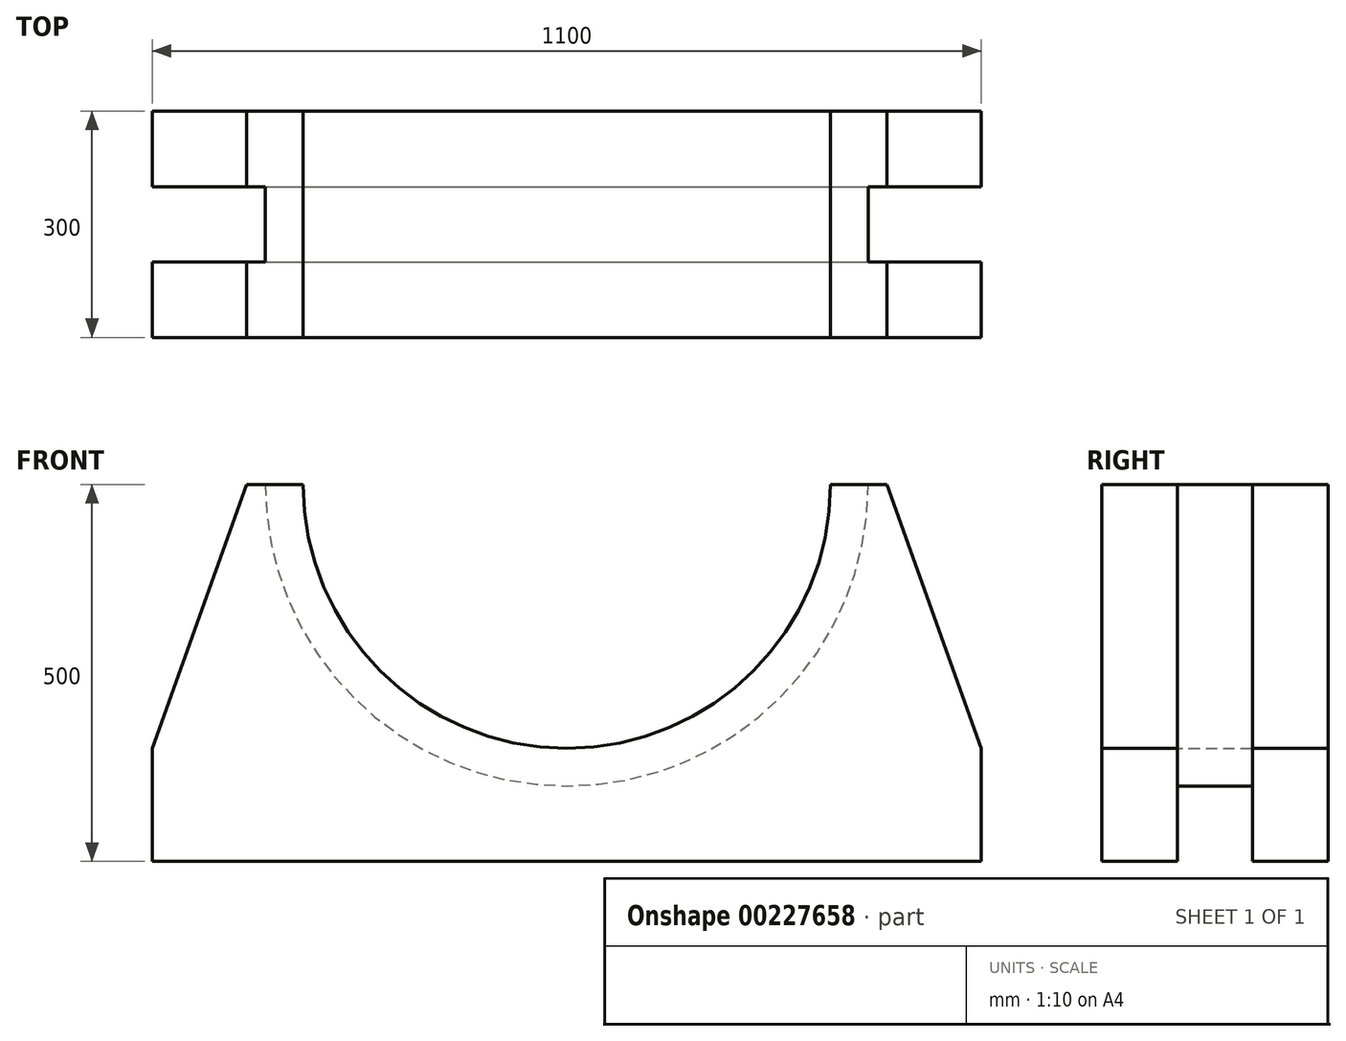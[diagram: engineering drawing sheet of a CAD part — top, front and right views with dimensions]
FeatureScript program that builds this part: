
annotation { "Feature Type Name" : "Feature", "Feature Type Description" : "" }
export const myFeature = defineFeature(function(context is Context, id is Id, definition is map)
    precondition{}
    {
        {
            var Q0;
            Q0=qCreatedBy(makeId("Front.planeOp"),FACE);
            var sketch = newSketch(context, id + "F0", { "sketchPlane" : qUnion([Q0])});
            skArc(sketch, "E0", {"start": v(-350, 0) * mm, "mid": v(-247.49, -247.49) * mm, "end": v(0, -350) * mm});
            skLineSegment(sketch, "E1", {"start": v(0, -696.52) * mm, "end": v(0, 518.58) * mm, "construction": true});
            skLineSegment(sketch, "E2", {"start": v(-350, 0) * mm, "end": v(-425, 0) * mm});
            skLineSegment(sketch, "E3", {"start": v(-425, 0) * mm, "end": v(-550, -350) * mm});
            skLineSegment(sketch, "E4", {"start": v(-550, -350) * mm, "end": v(-550, -500) * mm});
            skLineSegment(sketch, "E5", {"start": v(-550, -500) * mm, "end": v(0, -500) * mm});
            skLineSegment(sketch, "E6", {"start": v(0, -500) * mm, "end": v(0, -350) * mm});
            skLineSegment(sketch, "E7.MirrorCS", {"start": v(350, 0) * mm, "end": v(425, 0) * mm});
            skLineSegment(sketch, "E8.MirrorCS", {"start": v(550, -350) * mm, "end": v(550, -500) * mm});
            skLineSegment(sketch, "E9.MirrorCS", {"start": v(425, 0) * mm, "end": v(550, -350) * mm});
            skLineSegment(sketch, "E10.MirrorCS", {"start": v(550, -500) * mm, "end": v(0, -500) * mm});
            skArc(sketch, "E11.MirrorCS", {"start": v(350, 0) * mm, "mid": v(247.49, -247.49) * mm, "end": v(0, -350) * mm});
            skSolve(sketch);
        }
        {
            var Q0;
            Q0 = qSketchRegion(id + "F0", true);
            extrude(context, id + "F1", {"entities" : qUnion([Q0]), "endBound" : BoundingType.SYMMETRIC, "depth" : 300 * mm});
        }
        {
            var Q0;
            Q0=qCreatedBy(makeId("Front.planeOp"),FACE);
            var sketch = newSketch(context, id + "F2", { "sketchPlane" : qUnion([Q0])});
            skArc(sketch, "E12", {"start": v(-400, 0) * mm, "mid": v(0, -400) * mm, "end": v(400, 0) * mm});
            skLineSegment(sketch, "E13.0", {"start": v(-400, 0) * mm, "end": v(-425, 0) * mm});
            skLineSegment(sketch, "E14.0", {"start": v(-425, 0) * mm, "end": v(-550, -350) * mm});
            skLineSegment(sketch, "E15.0", {"start": v(-550, -350) * mm, "end": v(-550, -500) * mm});
            skLineSegment(sketch, "E16.0", {"start": v(-550, -500) * mm, "end": v(550, -500) * mm});
            skLineSegment(sketch, "E17.0", {"start": v(425, 0) * mm, "end": v(550, -350) * mm});
            skLineSegment(sketch, "E18.0", {"start": v(400, 0) * mm, "end": v(425, 0) * mm});
            skLineSegment(sketch, "E19", {"start": v(550, -350) * mm, "end": v(550, -500) * mm});
            skSolve(sketch);
        }
        {
            var Q0;
            Q0 = qSketchRegion(id + "F2", true);
            extrude(context, id + "F3", {"entities" : qUnion([Q0]), "operationType" : NewBodyOperationType.REMOVE, "endBound" : BoundingType.SYMMETRIC, "oppositeDirection" : true, "depth" : 100 * mm});
        }
    });
